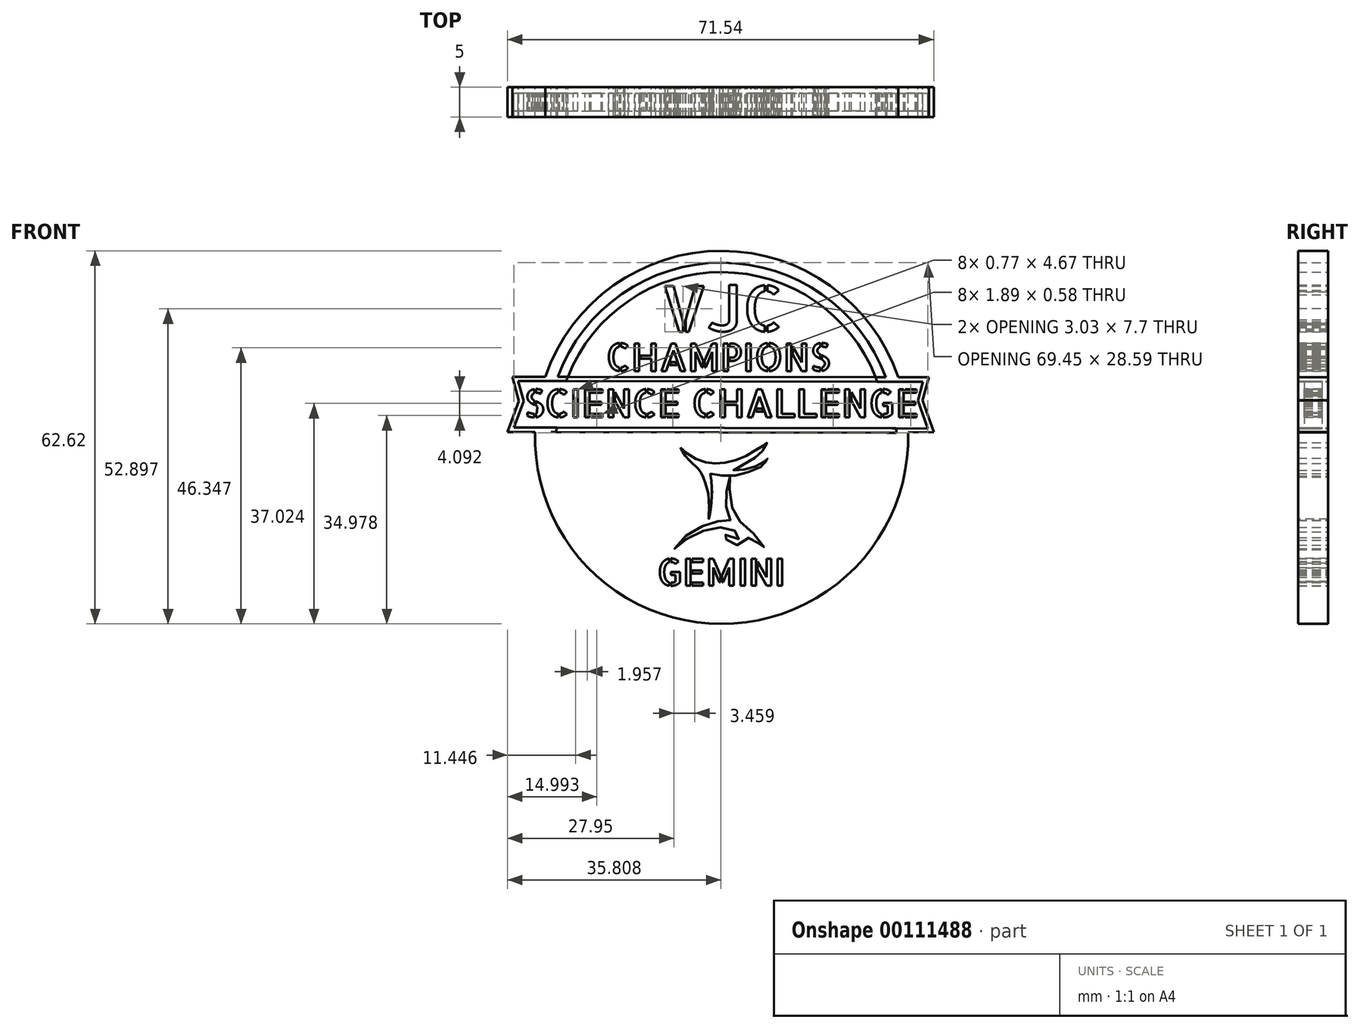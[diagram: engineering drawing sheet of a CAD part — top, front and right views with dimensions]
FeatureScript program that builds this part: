
annotation { "Feature Type Name" : "Feature", "Feature Type Description" : "" }
export const myFeature = defineFeature(function(context is Context, id is Id, definition is map)
    precondition{}
    {
        {
            var Q0;
            Q0=qCreatedBy(makeId("Front.planeOp"),FACE);
            var sketch = newSketch(context, id + "F0", { "sketchPlane" : qUnion([Q0])});
            skCircle(sketch, "E0", {"center": v(-0.65, -0.74) * mm, "radius": 27.74 * mm});
            skPoint(sketch, "E0.first.point", {"position": v(0, 27) * mm});
            skPoint(sketch, "E0.second.point", {"position": v(-1.07, -28.48) * mm});
            skPoint(sketch, "E0.third.point", {"position": v(-28.34, 0.92) * mm});
            skText(sketch, "E1", { "text": "CHAMPIONS", "fontName": "AllertaStencil-Regular.ttf"});
            skText(sketch, "E2", { "text": "GEMINI", "fontName": "AllertaStencil-Regular.ttf"});
            skLineSegment(sketch, "E3", {"start": v(-26.45, 9.45) * mm, "end": v(-35.78, 9.45) * mm});
            skLineSegment(sketch, "E4", {"start": v(-35.78, 9.45) * mm, "end": v(-34.66, 5.37) * mm});
            skLineSegment(sketch, "E5", {"start": v(-34.66, 5.37) * mm, "end": v(-36.58, 0.15) * mm});
            skLineSegment(sketch, "E6", {"start": v(-36.58, 0.15) * mm, "end": v(-28.38, 0.15) * mm});
            skLineSegment(sketch, "E7", {"start": v(25.2, 9.35) * mm, "end": v(34.13, 9.35) * mm});
            skLineSegment(sketch, "E8", {"start": v(34.13, 9.35) * mm, "end": v(33.08, 5.47) * mm});
            skLineSegment(sketch, "E9", {"start": v(33.08, 5.47) * mm, "end": v(34.96, 0.15) * mm});
            skLineSegment(sketch, "E10", {"start": v(34.96, 0.15) * mm, "end": v(27.09, 0) * mm});
            skFitSpline(sketch, "E11", {"points": [v(-7.58, -2.47) * mm, v(-6.81, -3.1) * mm, v(-5.48, -4.1) * mm, v(-4.07, -4.72) * mm, v(-2.43, -5.1) * mm, v(-1.24, -5.11) * mm, v(0.5, -4.9) * mm, v(2.28, -4.36) * mm, v(3.92, -3.59) * mm, v(5.25, -2.8) * mm, v(6.36, -2.09) * mm, v(6.6, -1.92) * mm, v(6.96, -1.63) * mm, v(6.55, -2.53) * mm, v(5.6, -3.57) * mm, v(3.6, -5.03) * mm, v(1.3, -6.2) * mm, v(2.4, -6.22) * mm, v(4.28, -5.87) * mm, v(6.18, -5) * mm, v(6.84, -4.5) * mm, v(7.02, -4.21) * mm, v(6.89, -4.9) * mm, v(4.88, -6.15) * mm, v(2.21, -7.02) * mm, v(-0.47, -7.17) * mm, v(-2.54, -6.8) * mm], "startDerivative": vector(22.31, -18.25) * mm, "endDerivative": vector(-43, 9.84) * mm});
            skFitSpline(sketch, "E12", {"points": [v(-7.58, -2.47) * mm, v(-6.77, -3.76) * mm, v(-5.4, -5.23) * mm, v(-4.6, -5.95) * mm, v(-3.85, -7.21) * mm, v(-3.12, -9.2) * mm, v(-2.76, -11.7) * mm, v(-2.79, -14.42) * mm, v(-2.53, -13.2) * mm, v(-2.27, -9.73) * mm, v(-2.5, -7.1) * mm, v(-2.54, -6.8) * mm], "startDerivative": vector(8.3, -15) * mm, "endDerivative": vector(-0.86, 6) * mm});
            skFitSpline(sketch, "E13", {"points": [v(0.75, -7.4) * mm, v(0.43, -8.37) * mm, v(0.09, -10.51) * mm, v(0.09, -12.04) * mm, v(0.48, -13.93) * mm, v(0.77, -14.7) * mm, v(0.24, -14.67) * mm, v(-1.6, -14.92) * mm, v(-3.24, -15.39) * mm, v(-5.56, -16.54) * mm, v(-7.6, -18.18) * mm, v(-8.54, -19.42) * mm, v(-7.5, -18.52) * mm, v(-5.25, -17.08) * mm, v(-2.87, -16.16) * mm, v(-0.75, -15.82) * mm, v(0.83, -16.04) * mm, v(2.13, -16.78) * mm, v(2.45, -17.43) * mm, v(1.87, -17.96) * mm, v(0.4, -17.56) * mm, v(-0.3, -16.62) * mm, v(-0.13, -17.55) * mm, v(0.77, -18.3) * mm, v(1.73, -18.77) * mm, v(3.25, -18.44) * mm, v(3.95, -17.55) * mm, v(4.8, -18.03) * mm, v(5.58, -18.58) * mm, v(6.56, -19.62) * mm, v(6.06, -18.43) * mm, v(4.7, -16.88) * mm, v(2.92, -15.28) * mm, v(1.75, -14.04) * mm, v(0.98, -11.93) * mm, v(0.66, -9.43) * mm, v(0.74, -8) * mm, v(0.75, -7.4) * mm]});
            skLineSegment(sketch, "E14", {"start": v(-26.45, 9.45) * mm, "end": v(26.52, 9.35) * mm});
            skLineSegment(sketch, "E15", {"start": v(-29.27, 0.15) * mm, "end": v(27.9, 0.02) * mm});
            skText(sketch, "E16", { "text": "SCIENCE CHALLENGE", "fontName": "AllertaStencil-Regular.ttf"});
            skText(sketch, "E17", { "text": "VJC", "fontName": "AllertaStencil-Regular.ttf"});
            skCircle(sketch, "E18.0", {"center": v(-0.65, -0.74) * mm, "radius": 29.33 * mm});
            skCircle(sketch, "E19.0", {"center": v(-0.65, -0.74) * mm, "radius": 31.31 * mm});
            skLineSegment(sketch, "E20.0", {"start": v(-26.45, 8.7) * mm, "end": v(26.52, 8.6) * mm});
            skLineSegment(sketch, "E21.0", {"start": v(-26.45, 8.7) * mm, "end": v(-34.8, 8.7) * mm});
            skLineSegment(sketch, "E22", {"start": v(26.52, 8.6) * mm, "end": v(33.15, 8.6) * mm});
            skLineSegment(sketch, "E23.0", {"start": v(-29.27, 0.9) * mm, "end": v(27.9, 0.77) * mm});
            skLineSegment(sketch, "E24", {"start": v(-29.27, 0.9) * mm, "end": v(-35.5, 0.92) * mm});
            skLineSegment(sketch, "E25", {"start": v(27.9, 0.77) * mm, "end": v(33.95, 0.75) * mm});
            skLineSegment(sketch, "E26.0", {"start": v(33.15, 8.6) * mm, "end": v(32.3, 5.44) * mm});
            skLineSegment(sketch, "E27.0", {"start": v(32.3, 5.44) * mm, "end": v(33.95, 0.75) * mm});
            skLineSegment(sketch, "E28.0", {"start": v(-33.88, 5.33) * mm, "end": v(-35.5, 0.92) * mm});
            skLineSegment(sketch, "E29.trimOffspring", {"start": v(-34.8, 8.7) * mm, "end": v(-33.88, 5.33) * mm});
            const initialGuessF0  = {"E1": [-0.02007, 0.01041, 1, 0, 0.00464], "E2": [-0.0115, -0.02564, 1, 0, 0.0045], "E16": [-0.0338, 0.00264, 1, 0, 0.00467], "E17": [-0.01077, 0.01704, 1, 0, 0.00766]};
            skSetInitialGuess(sketch, initialGuessF0);
            skSolve(sketch);
        }
        {
            var Q0;
            Q0=makeQuery(id+"F0.imprint","IMPRINT",FACE,{"disambiguationData":[TD([[makeQuery(id+"F0.imprint","IMPRINT",EDGE,{"derivedFrom":sQuery(id+"F0.wireOp",EDGE,"E2.sketch_text.stroke-0")}),1.0]])]});
            var Q1;
            Q1=makeQuery(id+"F0.imprint","IMPRINT",FACE,{"disambiguationData":[TD([[makeQuery(id+"F0.imprint","IMPRINT",EDGE,{"derivedFrom":sQuery(id+"F0.wireOp",EDGE,"E1.sketch_text.stroke-0")}),1.0]])]});
            var Q2;
            {var subQ18=sQuery(id+"F0.wireOp",EDGE,"E8");Q2=makeQuery(id+"F0.imprint","IMPRINT",FACE,{"disambiguationData":[TD([[makeQuery(id+"F0.imprint","IMPRINT",EDGE,{"derivedFrom":subQ18}),-1.0]])]});}
            var Q3;
            {var subQ13=sQuery(id+"F0.wireOp",EDGE,"E3");Q3=makeQuery(id+"F0.imprint","IMPRINT",FACE,{"disambiguationData":[TD([[makeQuery(id+"F0.imprint","IMPRINT",EDGE,{"derivedFrom":subQ13}),1.0]])]});}
            var Q4;
            {var subQ0=sQuery(id+"F0.wireOp",EDGE,"E19.0");var subQ1=sQuery(id+"F0.wireOp",EDGE,"E3");var subQ2=makeQuery(id+"F0.imprint","INTERSECT",VERTEX,{"derivedFrom":[subQ1,subQ0]});Q4=makeQuery(id+"F0.imprint","IMPRINT",FACE,{"disambiguationData":[TD([[makeQuery(id+"F0.imprint","IMPRINT",EDGE,{"disambiguationData":[TD([[subQ2,1.0]])],"derivedFrom":subQ1}),-1.0]])]});}
            var Q5;
            {var subQ0=sQuery(id+"F0.wireOp",EDGE,"E19.0");var subQ1=sQuery(id+"F0.wireOp",EDGE,"E6");var subQ2=makeQuery(id+"F0.imprint","INTERSECT",VERTEX,{"derivedFrom":[subQ1,subQ0]});Q5=makeQuery(id+"F0.imprint","IMPRINT",FACE,{"disambiguationData":[TD([[makeQuery(id+"F0.imprint","IMPRINT",EDGE,{"disambiguationData":[TD([[subQ2,-1.0]])],"derivedFrom":subQ1}),-1.0]])]});}
            var Q6;
            {var subQ18=sQuery(id+"F0.wireOp",EDGE,"E4");Q6=makeQuery(id+"F0.imprint","IMPRINT",FACE,{"disambiguationData":[TD([[makeQuery(id+"F0.imprint","IMPRINT",EDGE,{"derivedFrom":subQ18}),1.0]])]});}
            var Q7;
            {var subQ0=sQuery(id+"F0.wireOp",EDGE,"E19.0");var subQ1=sQuery(id+"F0.wireOp",EDGE,"E6");var subQ2=makeQuery(id+"F0.imprint","INTERSECT",VERTEX,{"derivedFrom":[subQ1,subQ0]});Q7=makeQuery(id+"F0.imprint","IMPRINT",FACE,{"disambiguationData":[TD([[makeQuery(id+"F0.imprint","IMPRINT",EDGE,{"disambiguationData":[TD([[subQ2,-1.0]])],"derivedFrom":subQ1}),1.0]])]});}
            var Q8;
            {var subQ0=sQuery(id+"F0.wireOp",EDGE,"E19.0");var subQ1=sQuery(id+"F0.wireOp",EDGE,"E10");var subQ2=makeQuery(id+"F0.imprint","INTERSECT",VERTEX,{"derivedFrom":[subQ1,subQ0]});Q8=makeQuery(id+"F0.imprint","IMPRINT",FACE,{"disambiguationData":[TD([[makeQuery(id+"F0.imprint","IMPRINT",EDGE,{"disambiguationData":[TD([[subQ2,-1.0]])],"derivedFrom":subQ1}),-1.0]])]});}
            var Q9;
            {var subQ0=sQuery(id+"F0.wireOp",EDGE,"E19.0");var subQ1=sQuery(id+"F0.wireOp",EDGE,"E7");var subQ2=makeQuery(id+"F0.imprint","INTERSECT",VERTEX,{"derivedFrom":[subQ1,subQ0]});Q9=makeQuery(id+"F0.imprint","IMPRINT",FACE,{"disambiguationData":[TD([[makeQuery(id+"F0.imprint","IMPRINT",EDGE,{"disambiguationData":[TD([[subQ2,1.0]])],"derivedFrom":subQ1}),-1.0]])]});}
            var Q10;
            {var subQ0=sQuery(id+"F0.wireOp",EDGE,"E6");var subQ1=sQuery(id+"F0.wireOp",EDGE,"E0");var subQ2=makeQuery(id+"F0.imprint","INTERSECT",VERTEX,{"derivedFrom":[subQ1,subQ0]});Q10=makeQuery(id+"F0.imprint","IMPRINT",FACE,{"disambiguationData":[TD([[makeQuery(id+"F0.imprint","IMPRINT",EDGE,{"disambiguationData":[TD([[subQ2,1.0]])],"derivedFrom":subQ1}),-1.0]])]});}
            var Q11;
            {var subQ3=sQuery(id+"F0.wireOp",EDGE,"E21.0");var subQ10=makeQuery(id+"F0.imprint","IMPRINT",VERTEX,{"derivedFrom":subQ3});Q11=makeQuery(id+"F0.imprint","IMPRINT",FACE,{"disambiguationData":[TD([[makeQuery(id+"F0.imprint","IMPRINT",EDGE,{"disambiguationData":[TD([[subQ10,1.0]])],"derivedFrom":subQ3}),-1.0]])]});}
            var Q12;
            {var subQ0=sQuery(id+"F0.wireOp",EDGE,"E15");var subQ1=sQuery(id+"F0.wireOp",EDGE,"E0");var subQ2=makeQuery(id+"F0.imprint","INTERSECT",VERTEX,{"disambiguationData":[OD(0.0)],"derivedFrom":[subQ1,subQ0]});Q12=makeQuery(id+"F0.imprint","IMPRINT",FACE,{"disambiguationData":[TD([[makeQuery(id+"F0.imprint","IMPRINT",EDGE,{"disambiguationData":[TD([[subQ2,-1.0]])],"derivedFrom":subQ1}),1.0]])]});}
            var Q13;
            {var subQ1=sQuery(id+"F0.wireOp",EDGE,"E7");var subQ6=sQuery(id+"F0.wireOp",EDGE,"E0");var subQ7=makeQuery(id+"F0.imprint","INTERSECT",VERTEX,{"derivedFrom":[subQ6,subQ1]});Q13=makeQuery(id+"F0.imprint","IMPRINT",FACE,{"disambiguationData":[TD([[makeQuery(id+"F0.imprint","IMPRINT",EDGE,{"disambiguationData":[TD([[subQ7,1.0]])],"derivedFrom":subQ6}),-1.0]])]});}
            var Q14;
            {var subQ0=sQuery(id+"F0.wireOp",EDGE,"E15");var subQ3=sQuery(id+"F0.wireOp",EDGE,"E0");var subQ4=makeQuery(id+"F0.imprint","INTERSECT",VERTEX,{"disambiguationData":[OD(0.0)],"derivedFrom":[subQ3,subQ0]});Q14=makeQuery(id+"F0.imprint","IMPRINT",FACE,{"disambiguationData":[TD([[makeQuery(id+"F0.imprint","IMPRINT",EDGE,{"disambiguationData":[TD([[subQ4,-1.0]])],"derivedFrom":subQ3}),-1.0]])]});}
            extrude(context, id + "F1", {"entities" : qUnion([Q0, Q1, Q2, Q3, Q4, Q5, Q6, Q7, Q8, Q9, Q10, Q11, Q12, Q13, Q14]), "endBound" : BoundingType.SYMMETRIC, "depth" : 5 * mm});
        }
        {
            var Q0;
            {var subQ11=sQuery(id+"F0.wireOp",EDGE,"E16.sketch_text.stroke-54");Q0=makeQuery(id+"F0.imprint","IMPRINT",FACE,{"disambiguationData":[TD([[makeQuery(id+"F0.imprint","IMPRINT",EDGE,{"derivedFrom":subQ11}),1.0]])]});}
            var Q1;
            {var subQ20=sQuery(id+"F0.wireOp",EDGE,"E16.sketch_text.stroke-1");Q1=makeQuery(id+"F0.imprint","IMPRINT",FACE,{"disambiguationData":[TD([[makeQuery(id+"F0.imprint","IMPRINT",EDGE,{"derivedFrom":subQ20}),1.0]])]});}
            var Q2;
            {var subQ18=sQuery(id+"F0.wireOp",EDGE,"E16.sketch_text.stroke-7");Q2=makeQuery(id+"F0.imprint","IMPRINT",FACE,{"disambiguationData":[TD([[makeQuery(id+"F0.imprint","IMPRINT",EDGE,{"derivedFrom":subQ18}),1.0]])]});}
            var Q3;
            {var subQ14=sQuery(id+"F0.wireOp",EDGE,"E16.sketch_text.stroke-51");Q3=makeQuery(id+"F0.imprint","IMPRINT",FACE,{"disambiguationData":[TD([[makeQuery(id+"F0.imprint","IMPRINT",EDGE,{"derivedFrom":subQ14}),1.0]])]});}
            var Q4;
            {var subQ1=sQuery(id+"F0.wireOp",EDGE,"E16.sketch_text.stroke-76");Q4=makeQuery(id+"F0.imprint","IMPRINT",FACE,{"disambiguationData":[TD([[makeQuery(id+"F0.imprint","IMPRINT",EDGE,{"derivedFrom":subQ1}),1.0]])]});}
            var Q5;
            {var subQ11=sQuery(id+"F0.wireOp",EDGE,"E16.sketch_text.stroke-289");Q5=makeQuery(id+"F0.imprint","IMPRINT",FACE,{"disambiguationData":[TD([[makeQuery(id+"F0.imprint","IMPRINT",EDGE,{"derivedFrom":subQ11}),1.0]])]});}
            var Q6;
            {var subQ12=sQuery(id+"F0.wireOp",EDGE,"E16.sketch_text.stroke-293");Q6=makeQuery(id+"F0.imprint","IMPRINT",FACE,{"disambiguationData":[TD([[makeQuery(id+"F0.imprint","IMPRINT",EDGE,{"derivedFrom":subQ12}),1.0]])]});}
            var Q7;
            {var subQ25=sQuery(id+"F0.wireOp",EDGE,"E16.sketch_text.stroke-246");Q7=makeQuery(id+"F0.imprint","IMPRINT",FACE,{"disambiguationData":[TD([[makeQuery(id+"F0.imprint","IMPRINT",EDGE,{"derivedFrom":subQ25}),1.0]])]});}
            var Q8;
            {var subQ0=sQuery(id+"F0.wireOp",EDGE,"E16.sketch_text.stroke-281");Q8=makeQuery(id+"F0.imprint","IMPRINT",FACE,{"disambiguationData":[TD([[makeQuery(id+"F0.imprint","IMPRINT",EDGE,{"derivedFrom":subQ0}),1.0]])]});}
            extrude(context, id + "F2", {"entities" : qUnion([Q0, Q1, Q2, Q3, Q4, Q5, Q6, Q7, Q8]), "endBound" : BoundingType.SYMMETRIC, "depth" : 3 * mm});
        }
    });
